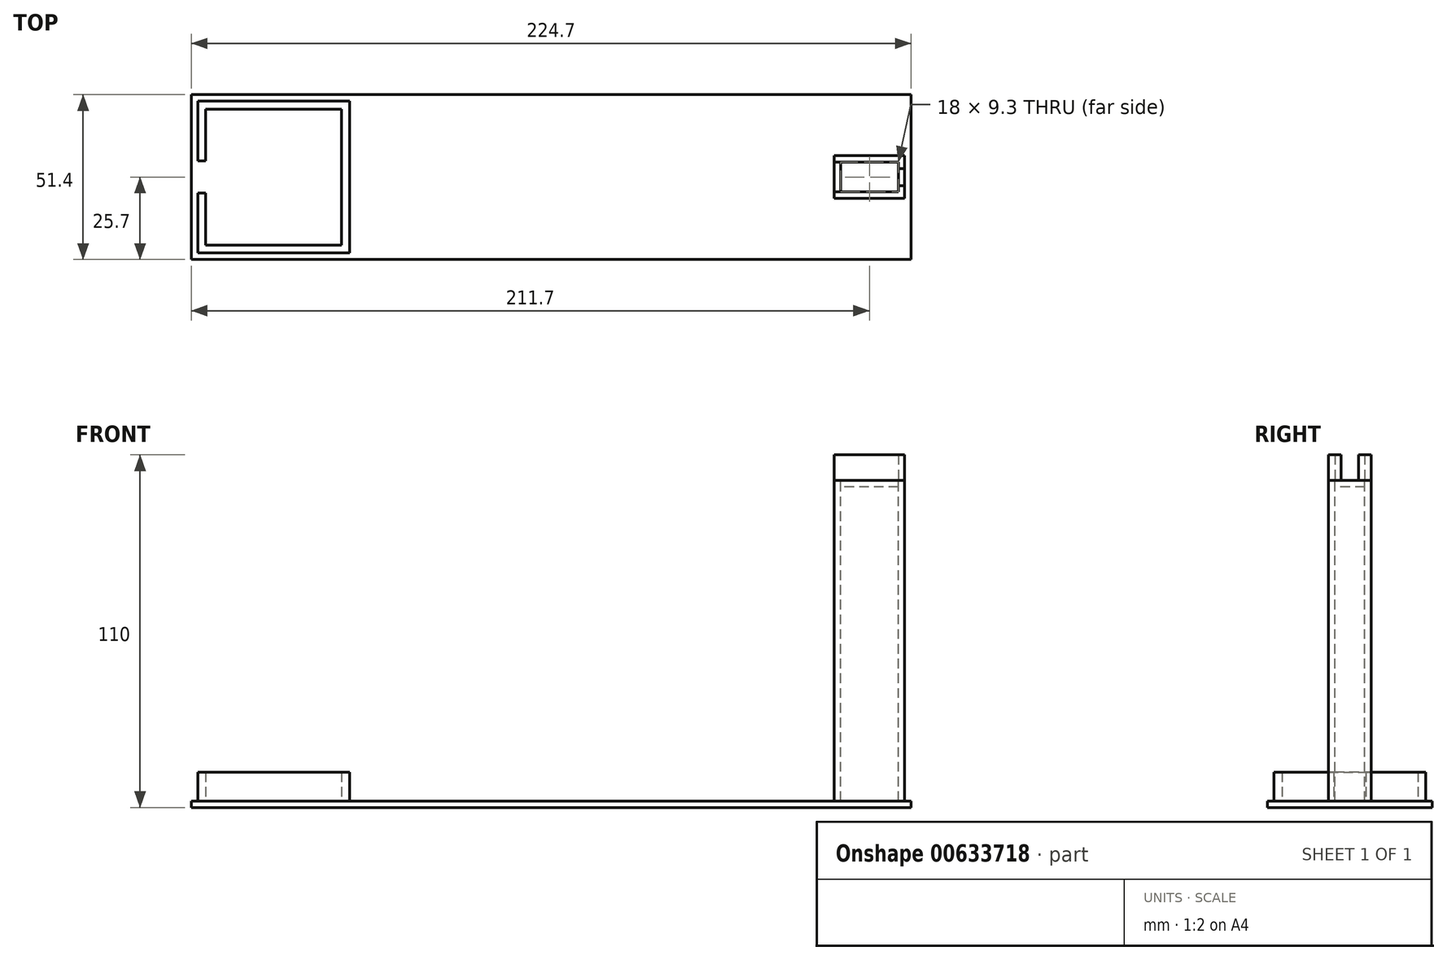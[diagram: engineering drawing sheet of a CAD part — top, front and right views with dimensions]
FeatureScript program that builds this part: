
annotation { "Feature Type Name" : "Feature", "Feature Type Description" : "" }
export const myFeature = defineFeature(function(context is Context, id is Id, definition is map)
    precondition{}
    {
        {
            var Q0;
            Q0=qCreatedBy(makeId("Top.planeOp"),FACE);
            var sketch = newSketch(context, id + "F0", { "sketchPlane" : qUnion([Q0])});
            skLineSegment(sketch, "E0.bottom", {"start": v(23.7, -23.7) * mm, "end": v(-23.7, -23.7) * mm});
            skLineSegment(sketch, "E0.top", {"start": v(23.7, 23.7) * mm, "end": v(-23.7, 23.7) * mm});
            skLineSegment(sketch, "E0.left", {"start": v(23.7, -23.7) * mm, "end": v(23.7, 23.7) * mm});
            skLineSegment(sketch, "E0.right", {"start": v(-23.7, -23.7) * mm, "end": v(-23.7, 23.7) * mm});
            skPoint(sketch, "E0.middle", {"position": v(0, 0) * mm});
            skLineSegment(sketch, "E1", {"start": v(-23.7, 0) * mm, "end": v(-23.7, 5) * mm});
            skLineSegment(sketch, "E2", {"start": v(-23.7, 5) * mm, "end": v(-21.2, 5) * mm});
            skLineSegment(sketch, "E3", {"start": v(-21.2, 5) * mm, "end": v(-21.2, -5) * mm});
            skLineSegment(sketch, "E4", {"start": v(-21.2, -5) * mm, "end": v(-23.7, -5) * mm});
            skLineSegment(sketch, "E5", {"start": v(-23.7, -5) * mm, "end": v(-23.7, 0) * mm});
            skLineSegment(sketch, "E6.bottom", {"start": v(21.2, 21.2) * mm, "end": v(-21.2, 21.2) * mm});
            skLineSegment(sketch, "E6.top", {"start": v(21.2, -21.2) * mm, "end": v(-21.2, -21.2) * mm});
            skLineSegment(sketch, "E6.left", {"start": v(21.2, 21.2) * mm, "end": v(21.2, -21.2) * mm});
            skLineSegment(sketch, "E6.right", {"start": v(-21.2, 21.2) * mm, "end": v(-21.2, -21.2) * mm});
            skLineSegment(sketch, "E7", {"start": v(0, 0) * mm, "end": v(175, 0) * mm});
            skSolve(sketch);
        }
        {
            var Q0;
            {var subQ6=sQuery(id+"F0.wireOp",EDGE,"E0.bottom");Q0=makeQuery(id+"F0.imprint","IMPRINT",FACE,{"disambiguationData":[TD([[makeQuery(id+"F0.imprint","IMPRINT",EDGE,{"derivedFrom":subQ6}),-1.0]])]});}
            var Q1;
            {var subQ2=sQuery(id+"F0.wireOp",EDGE,"E0.top");Q1=makeQuery(id+"F0.imprint","IMPRINT",FACE,{"disambiguationData":[TD([[makeQuery(id+"F0.imprint","IMPRINT",EDGE,{"derivedFrom":subQ2}),1.0]])]});}
            extrude(context, id + "F1", {"entities" : qUnion([Q0, Q1]), "depth" : 9 * mm, "offsetDistance" : 25 * mm});
        }
        {
            var Q0;
            Q0=sQuery(id+"F0.wireOp",VERTEX,"E7.end");
            var Q1;
            Q1=sQuery(id+"F0.wireOp",EDGE,"E7");
            cPlane(context, id + "F2", {"entities" : qUnion([Q0, Q1]), "cplaneType" : CPlaneType.LINE_POINT, "offset" : 25 * mm, "width" : 150 * mm, "height" : 150 * mm});
        }
        {
            var Q0;
            Q0=qCreatedBy(id+"F2.planeOp",FACE);
            var sketch = newSketch(context, id + "F3", { "sketchPlane" : qUnion([Q0])});
            skPoint(sketch, "E8.0", {"position": v(0, 0) * mm});
            skLineSegment(sketch, "E9", {"start": v(0, 0) * mm, "end": v(0, 100) * mm});
            skSolve(sketch);
        }
        {
            var Q0;
            Q0=sQuery(id+"F3.wireOp",EDGE,"E9");
            var Q1;
            Q1=sQuery(id+"F3.wireOp",VERTEX,"E9.end");
            cPlane(context, id + "F4", {"entities" : qUnion([Q0, Q1]), "cplaneType" : CPlaneType.LINE_POINT, "offset" : 25 * mm, "width" : 150 * mm, "height" : 150 * mm});
        }
        {
            var Q0;
            Q0=qCreatedBy(id+"F4.planeOp",FACE);
            var sketch = newSketch(context, id + "F5", { "sketchPlane" : qUnion([Q0])});
            skPoint(sketch, "E10.0", {"position": v(175, 0) * mm});
            skLineSegment(sketch, "E11", {"start": v(175, 0) * mm, "end": v(185, 0) * mm});
            skLineSegment(sketch, "E12.bottom", {"start": v(195, 4.65) * mm, "end": v(175, 4.65) * mm});
            skLineSegment(sketch, "E12.top", {"start": v(195, -4.65) * mm, "end": v(175, -4.65) * mm});
            skLineSegment(sketch, "E12.left", {"start": v(195, 4.65) * mm, "end": v(195, -4.65) * mm});
            skLineSegment(sketch, "E12.right", {"start": v(175, 4.65) * mm, "end": v(175, -4.65) * mm});
            skPoint(sketch, "E12.middle", {"position": v(185, 0) * mm});
            skLineSegment(sketch, "E13.0", {"start": v(197, 6.65) * mm, "end": v(175, 6.65) * mm});
            skLineSegment(sketch, "E13.1", {"start": v(197, 6.65) * mm, "end": v(197, -6.65) * mm});
            skLineSegment(sketch, "E13.2", {"start": v(197, -6.65) * mm, "end": v(175, -6.65) * mm});
            skLineSegment(sketch, "E14", {"start": v(195, 0) * mm, "end": v(197, 0) * mm});
            skLineSegment(sketch, "E15.bottom", {"start": v(197, -2.7) * mm, "end": v(195, -2.7) * mm});
            skLineSegment(sketch, "E15.top", {"start": v(197, 2.7) * mm, "end": v(195, 2.7) * mm});
            skLineSegment(sketch, "E15.left", {"start": v(197, -2.7) * mm, "end": v(197, 2.7) * mm});
            skLineSegment(sketch, "E15.right", {"start": v(195, -2.7) * mm, "end": v(195, 2.7) * mm});
            skPoint(sketch, "E15.middle", {"position": v(196, 0) * mm});
            skLineSegment(sketch, "E16", {"start": v(175, -6.65) * mm, "end": v(175, 6.65) * mm});
            skLineSegment(sketch, "E17.0", {"start": v(177, -6.65) * mm, "end": v(177, 6.65) * mm});
            skSolve(sketch);
        }
        {
            var Q0;
            {var subQ3=sQuery(id+"F5.wireOp",EDGE,"E15.bottom");Q0=makeQuery(id+"F5.imprint","IMPRINT",FACE,{"disambiguationData":[TD([[makeQuery(id+"F5.imprint","IMPRINT",EDGE,{"derivedFrom":subQ3}),1.0]])]});}
            var Q1;
            {var subQ3=sQuery(id+"F5.wireOp",EDGE,"E15.top");Q1=makeQuery(id+"F5.imprint","IMPRINT",FACE,{"disambiguationData":[TD([[makeQuery(id+"F5.imprint","IMPRINT",EDGE,{"derivedFrom":subQ3}),-1.0]])]});}
            var Q2;
            {var subQ0=sQuery(id+"F5.wireOp",EDGE,"E16");var subQ1=sQuery(id+"F5.wireOp",EDGE,"E12.bottom");var subQ2=makeQuery(id+"F5.imprint","INTERSECT",VERTEX,{"derivedFrom":[subQ1,subQ0]});Q2=makeQuery(id+"F5.imprint","IMPRINT",FACE,{"disambiguationData":[TD([[makeQuery(id+"F5.imprint","IMPRINT",EDGE,{"disambiguationData":[TD([[subQ2,1.0]])],"derivedFrom":subQ1}),-1.0]])]});}
            var Q3;
            {var subQ0=sQuery(id+"F5.wireOp",EDGE,"E16");var subQ1=sQuery(id+"F5.wireOp",EDGE,"E12.top");var subQ2=makeQuery(id+"F5.imprint","INTERSECT",VERTEX,{"derivedFrom":[subQ1,subQ0]});Q3=makeQuery(id+"F5.imprint","IMPRINT",FACE,{"disambiguationData":[TD([[makeQuery(id+"F5.imprint","IMPRINT",EDGE,{"disambiguationData":[TD([[subQ2,1.0]])],"derivedFrom":subQ1}),1.0]])]});}
            extrude(context, id + "F6", {"entities" : qUnion([Q0, Q1, Q2, Q3]), "depth" : 8 * mm, "offsetDistance" : 25 * mm});
        }
        {
            var Q0;
            {var subQ0=sQuery(id+"F5.wireOp",EDGE,"E12.left");var subQ1=sQuery(id+"F5.wireOp",EDGE,"E12.bottom");var subQ2=makeQuery(id+"F5.imprint","INTERSECT",VERTEX,{"derivedFrom":[subQ1,subQ0]});Q0=makeQuery(id+"F5.imprint","IMPRINT",FACE,{"disambiguationData":[TD([[makeQuery(id+"F5.imprint","IMPRINT",EDGE,{"disambiguationData":[TD([[subQ2,-1.0]])],"derivedFrom":subQ1}),1.0]])]});}
            extrude(context, id + "F7", {"entities" : qUnion([Q0]), "oppositeDirection" : true, "depth" : 2 * mm, "offsetDistance" : 25 * mm});
        }
        {
            var Q0;
            {var subQ3=sQuery(id+"F5.wireOp",EDGE,"E15.bottom");Q0=makeQuery(id+"F5.imprint","IMPRINT",FACE,{"disambiguationData":[TD([[makeQuery(id+"F5.imprint","IMPRINT",EDGE,{"derivedFrom":subQ3}),1.0]])]});}
            var Q1;
            {var subQ0=sQuery(id+"F5.wireOp",EDGE,"E16");var subQ1=sQuery(id+"F5.wireOp",EDGE,"E12.top");var subQ2=makeQuery(id+"F5.imprint","INTERSECT",VERTEX,{"derivedFrom":[subQ1,subQ0]});Q1=makeQuery(id+"F5.imprint","IMPRINT",FACE,{"disambiguationData":[TD([[makeQuery(id+"F5.imprint","IMPRINT",EDGE,{"disambiguationData":[TD([[subQ2,1.0]])],"derivedFrom":subQ1}),1.0]])]});}
            var Q2;
            {var subQ0=sQuery(id+"F5.wireOp",EDGE,"E16");var subQ1=sQuery(id+"F5.wireOp",EDGE,"E11");var subQ2=makeQuery(id+"F5.imprint","INTERSECT",VERTEX,{"derivedFrom":[subQ1,subQ0]});Q2=makeQuery(id+"F5.imprint","IMPRINT",FACE,{"disambiguationData":[TD([[makeQuery(id+"F5.imprint","IMPRINT",EDGE,{"disambiguationData":[TD([[subQ2,-1.0]])],"derivedFrom":subQ1}),-1.0]])]});}
            var Q3;
            {var subQ0=sQuery(id+"F5.wireOp",EDGE,"E16");var subQ1=sQuery(id+"F5.wireOp",EDGE,"E11");var subQ2=makeQuery(id+"F5.imprint","INTERSECT",VERTEX,{"derivedFrom":[subQ1,subQ0]});Q3=makeQuery(id+"F5.imprint","IMPRINT",FACE,{"disambiguationData":[TD([[makeQuery(id+"F5.imprint","IMPRINT",EDGE,{"disambiguationData":[TD([[subQ2,-1.0]])],"derivedFrom":subQ1}),1.0]])]});}
            var Q4;
            {var subQ0=sQuery(id+"F5.wireOp",EDGE,"E16");var subQ1=sQuery(id+"F5.wireOp",EDGE,"E12.bottom");var subQ2=makeQuery(id+"F5.imprint","INTERSECT",VERTEX,{"derivedFrom":[subQ1,subQ0]});Q4=makeQuery(id+"F5.imprint","IMPRINT",FACE,{"disambiguationData":[TD([[makeQuery(id+"F5.imprint","IMPRINT",EDGE,{"disambiguationData":[TD([[subQ2,1.0]])],"derivedFrom":subQ1}),-1.0]])]});}
            var Q5;
            {var subQ3=sQuery(id+"F5.wireOp",EDGE,"E15.top");Q5=makeQuery(id+"F5.imprint","IMPRINT",FACE,{"disambiguationData":[TD([[makeQuery(id+"F5.imprint","IMPRINT",EDGE,{"derivedFrom":subQ3}),-1.0]])]});}
            var Q6;
            {var subQ0=sQuery(id+"F5.wireOp",EDGE,"E14");Q6=makeQuery(id+"F5.imprint","IMPRINT",FACE,{"disambiguationData":[TD([[makeQuery(id+"F5.imprint","IMPRINT",EDGE,{"derivedFrom":subQ0}),-1.0]])]});}
            var Q7;
            {var subQ0=sQuery(id+"F5.wireOp",EDGE,"E14");Q7=makeQuery(id+"F5.imprint","IMPRINT",FACE,{"disambiguationData":[TD([[makeQuery(id+"F5.imprint","IMPRINT",EDGE,{"derivedFrom":subQ0}),1.0]])]});}
            extrude(context, id + "F8", {"entities" : qUnion([Q0, Q1, Q2, Q3, Q4, Q5, Q6, Q7]), "oppositeDirection" : true, "depth" : 100 * mm, "offsetDistance" : 25 * mm});
        }
        {
            var Q0;
            Q0=qCreatedBy(makeId("Top.planeOp"),FACE);
            var sketch = newSketch(context, id + "F9", { "sketchPlane" : qUnion([Q0])});
            skPoint(sketch, "E18.0", {"position": v(-23.7, -23.7) * mm});
            skPoint(sketch, "E19.0", {"position": v(-23.7, 23.7) * mm});
            skPoint(sketch, "E20.0", {"position": v(197, 6.65) * mm});
            skLineSegment(sketch, "E21", {"start": v(-23.7, 23.7) * mm, "end": v(197, 23.7) * mm});
            skLineSegment(sketch, "E22", {"start": v(197, 23.7) * mm, "end": v(197, -23.7) * mm});
            skLineSegment(sketch, "E23", {"start": v(197, -23.7) * mm, "end": v(-23.7, -23.7) * mm});
            skLineSegment(sketch, "E24", {"start": v(-23.7, 23.7) * mm, "end": v(-23.7, -23.7) * mm});
            skLineSegment(sketch, "E25.0", {"start": v(199, -25.7) * mm, "end": v(-25.7, -25.7) * mm});
            skLineSegment(sketch, "E25.1", {"start": v(199, 25.7) * mm, "end": v(199, -25.7) * mm});
            skLineSegment(sketch, "E25.2", {"start": v(-25.7, 25.7) * mm, "end": v(199, 25.7) * mm});
            skLineSegment(sketch, "E25.3", {"start": v(-25.7, 25.7) * mm, "end": v(-25.7, -25.7) * mm});
            skSolve(sketch);
        }
        {
            var Q0;
            Q0=makeQuery(id+"F9.imprint","IMPRINT",FACE,{"disambiguationData":[TD([[makeQuery(id+"F9.imprint","IMPRINT",EDGE,{"derivedFrom":sQuery(id+"F9.wireOp",EDGE,"E21")}),1.0]])]});
            var Q1;
            Q1=makeQuery(id+"F9.imprint","IMPRINT",FACE,{"disambiguationData":[TD([[makeQuery(id+"F9.imprint","IMPRINT",EDGE,{"derivedFrom":sQuery(id+"F9.wireOp",EDGE,"E21")}),-1.0]])]});
            extrude(context, id + "F10", {"entities" : qUnion([Q0, Q1]), "oppositeDirection" : true, "depth" : 2 * mm, "offsetDistance" : 25 * mm});
        }
    });
